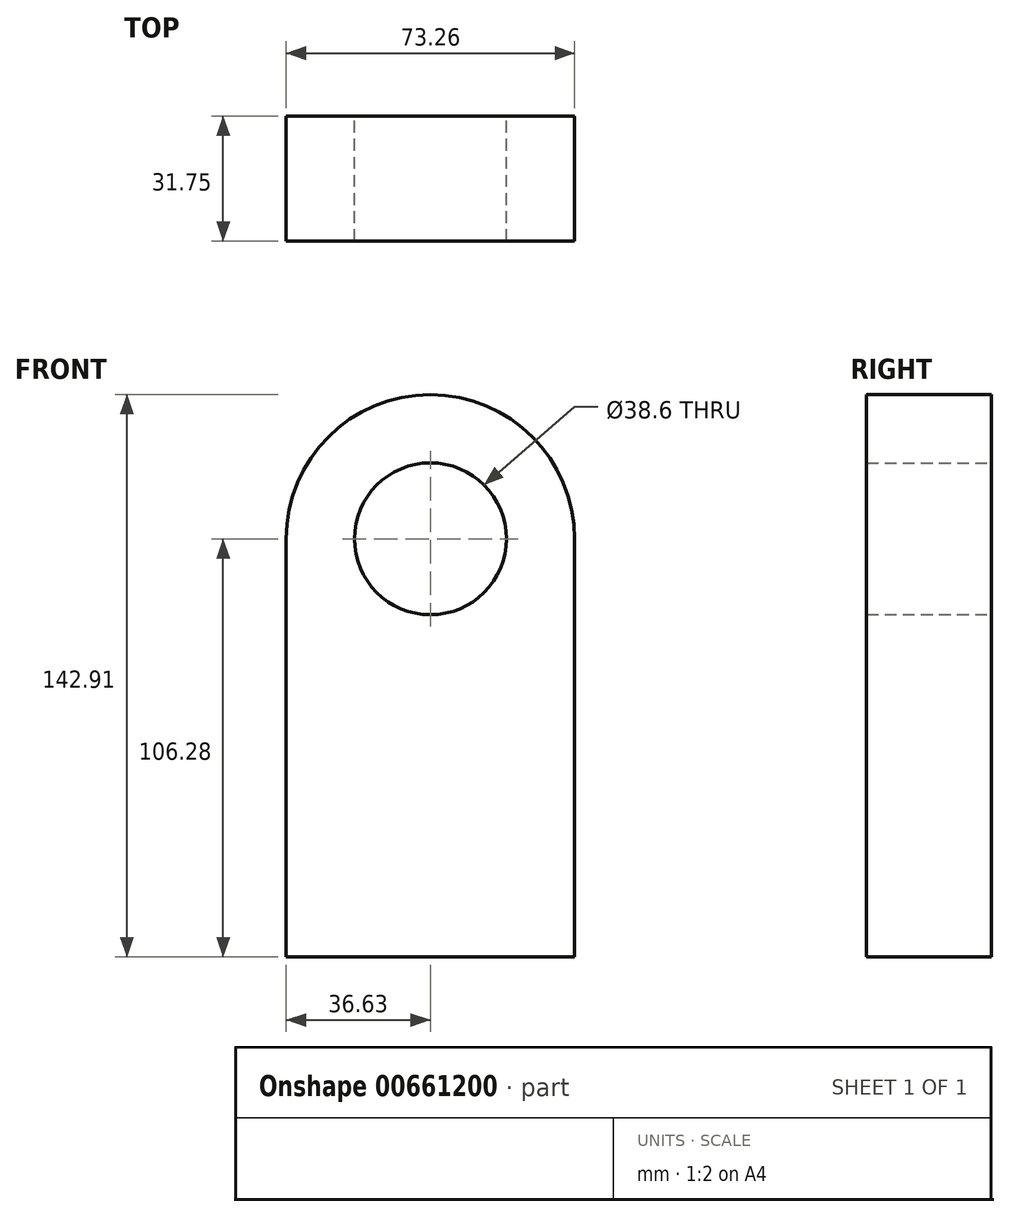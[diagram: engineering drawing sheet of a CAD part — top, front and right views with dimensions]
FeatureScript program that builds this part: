
annotation { "Feature Type Name" : "Feature", "Feature Type Description" : "" }
export const myFeature = defineFeature(function(context is Context, id is Id, definition is map)
    precondition{}
    {
        {
            var Q0;
            Q0=qCreatedBy(makeId("Front.planeOp"),FACE);
            var sketch = newSketch(context, id + "F0", { "sketchPlane" : qUnion([Q0])});
            skLineSegment(sketch, "E0.bottom", {"start": v(36.63, 53.14) * mm, "end": v(-36.63, 53.14) * mm});
            skLineSegment(sketch, "E0.top", {"start": v(36.63, -53.14) * mm, "end": v(-36.63, -53.14) * mm});
            skLineSegment(sketch, "E0.left", {"start": v(36.63, 53.14) * mm, "end": v(36.63, -53.14) * mm});
            skLineSegment(sketch, "E0.right", {"start": v(-36.63, 53.14) * mm, "end": v(-36.63, -53.14) * mm});
            skPoint(sketch, "E0.middle", {"position": v(0, 0) * mm});
            skArc(sketch, "E1", {"start": v(36.63, 53.14) * mm, "mid": v(0, 89.77) * mm, "end": v(-36.63, 53.14) * mm});
            skCircle(sketch, "E2", {"center": v(0, 53.14) * mm, "radius": 19.3 * mm});
            skSolve(sketch);
        }
        {
            var Q0;
            Q0=makeQuery(id+"F0.imprint","IMPRINT",FACE,{"disambiguationData":[TD([[makeQuery(id+"F0.imprint","IMPRINT",EDGE,{"derivedFrom":sQuery(id+"F0.wireOp",EDGE,"E0.top")}),-1.0]])]});
            var Q1;
            {var subQ0=sQuery(id+"F0.wireOp",EDGE,"E1");Q1=makeQuery(id+"F0.imprint","IMPRINT",FACE,{"disambiguationData":[TD([[makeQuery(id+"F0.imprint","IMPRINT",EDGE,{"derivedFrom":subQ0}),1.0]])]});}
            extrude(context, id + "F1", {"entities" : qUnion([Q0, Q1]), "depth" : 31.75 * mm, "offsetDistance" : 25.4 * mm});
        }
    });
